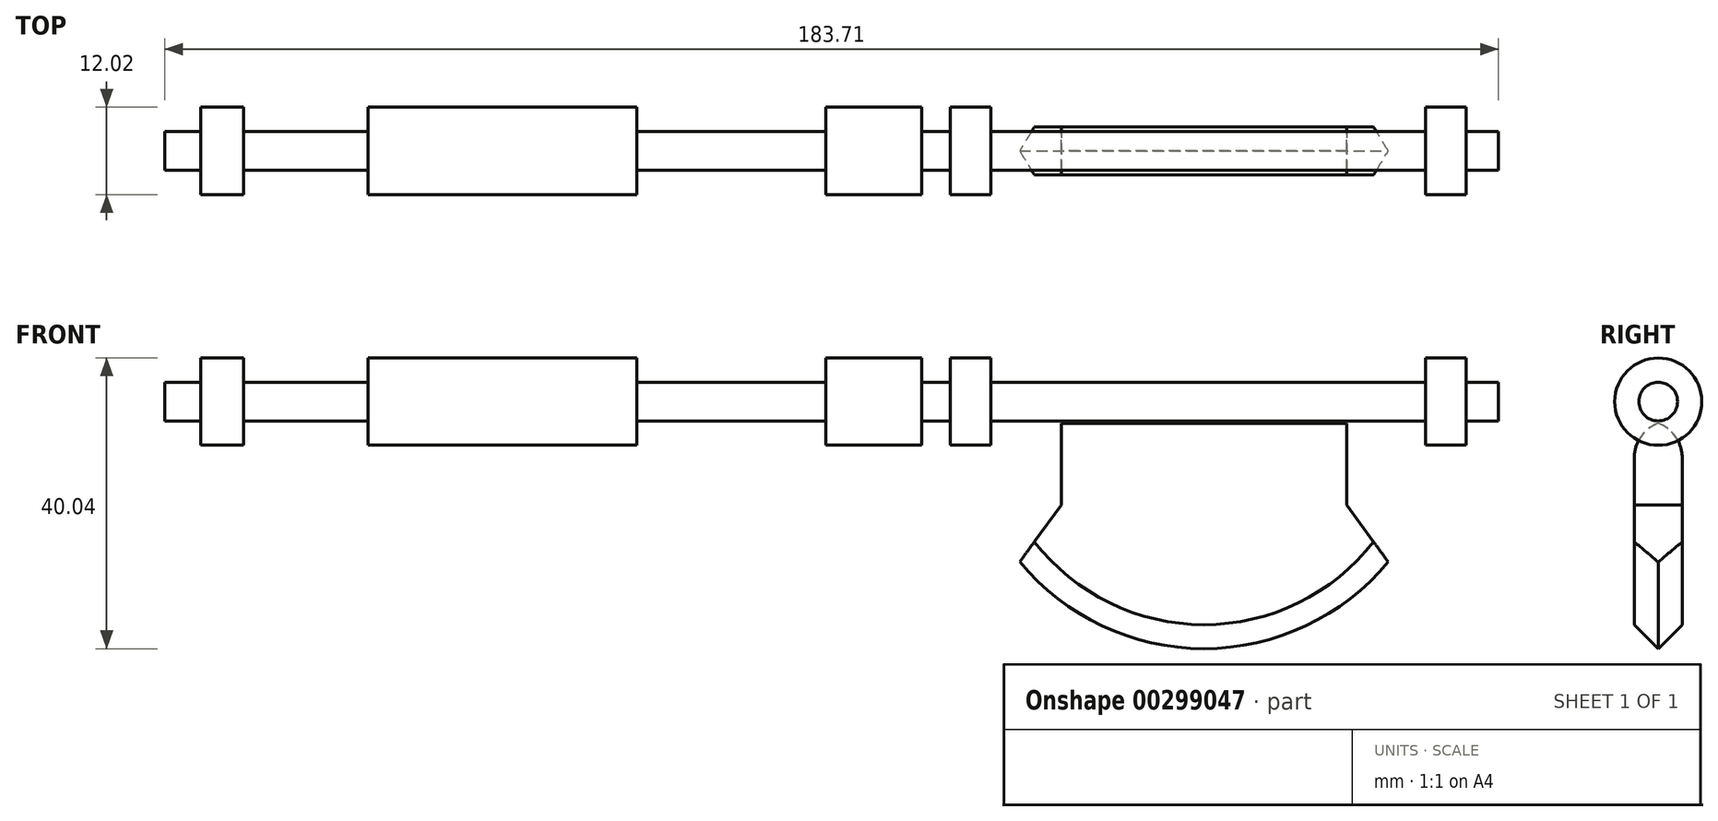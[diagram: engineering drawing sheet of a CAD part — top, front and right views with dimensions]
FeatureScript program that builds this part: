
annotation { "Feature Type Name" : "Feature", "Feature Type Description" : "" }
export const myFeature = defineFeature(function(context is Context, id is Id, definition is map)
    precondition{}
    {
        {
            var Q0;
            Q0=qCreatedBy(makeId("Front.planeOp"),FACE);
            var sketch = newSketch(context, id + "F0", { "sketchPlane" : qUnion([Q0])});
            skLineSegment(sketch, "E0", {"start": v(-57.35, 7.1) * mm, "end": v(-57.35, 12.42) * mm});
            skLineSegment(sketch, "E1", {"start": v(-57.35, 12.42) * mm, "end": v(-52.42, 12.42) * mm});
            skLineSegment(sketch, "E2", {"start": v(-52.42, 12.42) * mm, "end": v(-52.42, 15.77) * mm});
            skLineSegment(sketch, "E3", {"start": v(-46.5, 15.77) * mm, "end": v(-52.42, 15.77) * mm});
            skLineSegment(sketch, "E4", {"start": v(-46.5, 15.77) * mm, "end": v(-46.5, 12.42) * mm});
            skLineSegment(sketch, "E5", {"start": v(-46.5, 12.42) * mm, "end": v(-29.36, 12.42) * mm});
            skLineSegment(sketch, "E6", {"start": v(-29.36, 12.42) * mm, "end": v(-29.36, 15.77) * mm});
            skLineSegment(sketch, "E7", {"start": v(-29.36, 15.77) * mm, "end": v(7.69, 15.77) * mm});
            skLineSegment(sketch, "E8", {"start": v(7.69, 15.77) * mm, "end": v(7.69, 12.42) * mm});
            skLineSegment(sketch, "E9", {"start": v(7.69, 12.42) * mm, "end": v(33.73, 12.42) * mm});
            skLineSegment(sketch, "E10", {"start": v(33.73, 12.42) * mm, "end": v(33.73, 15.77) * mm});
            skLineSegment(sketch, "E11", {"start": v(33.73, 15.77) * mm, "end": v(46.93, 15.77) * mm});
            skLineSegment(sketch, "E12", {"start": v(46.93, 15.77) * mm, "end": v(46.93, 12.42) * mm});
            skLineSegment(sketch, "E13", {"start": v(46.93, 12.42) * mm, "end": v(50.84, 12.42) * mm});
            skLineSegment(sketch, "E14", {"start": v(50.84, 12.42) * mm, "end": v(50.84, 15.77) * mm});
            skLineSegment(sketch, "E15", {"start": v(50.84, 15.77) * mm, "end": v(56.42, 15.77) * mm});
            skLineSegment(sketch, "E16", {"start": v(56.42, 15.77) * mm, "end": v(56.42, 12.42) * mm});
            skLineSegment(sketch, "E17", {"start": v(56.42, 12.42) * mm, "end": v(116.31, 12.42) * mm});
            skLineSegment(sketch, "E18", {"start": v(116.31, 12.42) * mm, "end": v(116.31, 15.77) * mm});
            skLineSegment(sketch, "E19", {"start": v(116.31, 15.77) * mm, "end": v(121.9, 15.77) * mm});
            skLineSegment(sketch, "E20", {"start": v(121.9, 15.77) * mm, "end": v(121.9, 12.42) * mm});
            skLineSegment(sketch, "E21", {"start": v(121.9, 12.42) * mm, "end": v(126.36, 12.42) * mm});
            skLineSegment(sketch, "E22.MirrorCS", {"start": v(56.42, 7.1) * mm, "end": v(116.31, 7.1) * mm});
            skLineSegment(sketch, "E23.MirrorCS", {"start": v(116.31, 7.1) * mm, "end": v(116.31, 3.74) * mm});
            skLineSegment(sketch, "E24.MirrorCS", {"start": v(116.31, 3.74) * mm, "end": v(121.9, 3.74) * mm});
            skLineSegment(sketch, "E25.MirrorCS", {"start": v(121.9, 3.74) * mm, "end": v(121.9, 7.1) * mm});
            skLineSegment(sketch, "E26.MirrorCS", {"start": v(121.9, 7.1) * mm, "end": v(126.36, 7.1) * mm});
            skLineSegment(sketch, "E27.MirrorCS", {"start": v(56.42, 3.74) * mm, "end": v(56.42, 7.1) * mm});
            skLineSegment(sketch, "E28.MirrorCS", {"start": v(50.84, 3.74) * mm, "end": v(56.42, 3.74) * mm});
            skLineSegment(sketch, "E29.MirrorCS", {"start": v(50.84, 7.1) * mm, "end": v(50.84, 3.74) * mm});
            skLineSegment(sketch, "E30.MirrorCS", {"start": v(46.93, 7.1) * mm, "end": v(50.84, 7.1) * mm});
            skLineSegment(sketch, "E31.MirrorCS", {"start": v(46.93, 3.74) * mm, "end": v(46.93, 7.1) * mm});
            skLineSegment(sketch, "E32.MirrorCS", {"start": v(33.73, 3.74) * mm, "end": v(46.93, 3.74) * mm});
            skLineSegment(sketch, "E33.MirrorCS", {"start": v(33.73, 7.1) * mm, "end": v(33.73, 3.74) * mm});
            skLineSegment(sketch, "E34.MirrorCS", {"start": v(7.69, 7.1) * mm, "end": v(33.73, 7.1) * mm});
            skLineSegment(sketch, "E35.MirrorCS", {"start": v(7.69, 3.74) * mm, "end": v(7.69, 7.1) * mm});
            skLineSegment(sketch, "E36.MirrorCS", {"start": v(-29.36, 3.74) * mm, "end": v(7.69, 3.74) * mm});
            skLineSegment(sketch, "E37.MirrorCS", {"start": v(-29.36, 7.1) * mm, "end": v(-29.36, 3.74) * mm});
            skLineSegment(sketch, "E38.MirrorCS", {"start": v(-46.5, 7.1) * mm, "end": v(-29.36, 7.1) * mm});
            skLineSegment(sketch, "E39.MirrorCS", {"start": v(-46.5, 3.74) * mm, "end": v(-46.5, 7.1) * mm});
            skLineSegment(sketch, "E40.MirrorCS", {"start": v(-46.5, 3.74) * mm, "end": v(-52.42, 3.74) * mm});
            skLineSegment(sketch, "E41.MirrorCS", {"start": v(-52.42, 7.1) * mm, "end": v(-52.42, 3.74) * mm});
            skLineSegment(sketch, "E42.MirrorCS", {"start": v(-57.35, 7.1) * mm, "end": v(-52.42, 7.1) * mm});
            skLineSegment(sketch, "E43", {"start": v(126.36, 12.42) * mm, "end": v(126.36, 7.1) * mm});
            skLineSegment(sketch, "E44", {"start": v(-57.35, 9.75) * mm, "end": v(126.36, 9.75) * mm});
            skLineSegment(sketch, "E45", {"start": v(66.13, 7.1) * mm, "end": v(66.13, -4.45) * mm});
            skLineSegment(sketch, "E46", {"start": v(66.13, -4.45) * mm, "end": v(59.34, -13.8) * mm});
            skLineSegment(sketch, "E47", {"start": v(105.45, 7.1) * mm, "end": v(105.45, -4.45) * mm});
            skLineSegment(sketch, "E48", {"start": v(105.45, -4.45) * mm, "end": v(112.25, -13.8) * mm});
            skArc(sketch, "E49", {"start": v(59.34, -13.8) * mm, "mid": v(85.8, -26.04) * mm, "end": v(112.25, -13.8) * mm});
            skSolve(sketch);
        }
        {
            var Q0;
            {var subQ1=sQuery(id+"F0.wireOp",EDGE,"E1");Q0=makeQuery(id+"F0.imprint","IMPRINT",FACE,{"disambiguationData":[TD([[makeQuery(id+"F0.imprint","IMPRINT",EDGE,{"derivedFrom":subQ1}),-1.0]])]});}
            var Q1;
            Q1=sQuery(id+"F0.wireOp",EDGE,"E44");
            revolve(context, id + "F1", {"entities" : qUnion([Q0]), "axis" : qUnion([Q1]), "revolveType" : RevolveType.FULL});
        }
        {
            var Q0;
            {var subQ1=sQuery(id+"F0.wireOp",EDGE,"E45");Q0=makeQuery(id+"F0.imprint","IMPRINT",FACE,{"disambiguationData":[TD([[makeQuery(id+"F0.imprint","IMPRINT",EDGE,{"derivedFrom":subQ1}),1.0]])]});}
            var Q1;
            Q1=sQuery(id+"F0.wireOp",EDGE,"E45");
            var Q2;
            Q2=sQuery(id+"F0.wireOp",EDGE,"E47");
            var Q3;
            Q3=sQuery(id+"F0.wireOp",EDGE,"E48");
            var Q4;
            Q4=sQuery(id+"F0.wireOp",EDGE,"E49");
            var Q5;
            Q5=sQuery(id+"F0.wireOp",EDGE,"E46");
            extrude(context, id + "F2", {"entities" : qUnion([Q0]), "surfaceEntities" : qUnion([Q1, Q2, Q3, Q4, Q5]), "oppositeDirection" : true, "depth" : 3.3 * mm});
        }
        {
            var Q0;
            Q0=makeQuery(id+"F2.opExtrude","CAP_FACE",FACE,{"disambiguationData":[OSD([sQuery(id+"F0.wireOp",EDGE,"E22.MirrorCS"),sQuery(id+"F0.wireOp",EDGE,"E45"),sQuery(id+"F0.wireOp",EDGE,"E46"),sQuery(id+"F0.wireOp",EDGE,"E47"),sQuery(id+"F0.wireOp",EDGE,"E48"),sQuery(id+"F0.wireOp",EDGE,"E49")])],"isStart":true});
            extrude(context, id + "F3", {"entities" : qUnion([Q0]), "operationType" : NewBodyOperationType.ADD, "depth" : 3.3 * mm});
        }
        {
            var Q0;
            Q0=makeQuery(id+"F3.opExtrude","CAP_EDGE",EDGE,{"disambiguationData":[OSD([sQuery(id+"F0.wireOp",EDGE,"E49")])],"isStart":false});
            var Q1;
            Q1=makeQuery(id+"F2.opExtrude","CAP_EDGE",EDGE,{"disambiguationData":[OSD([sQuery(id+"F0.wireOp",EDGE,"E49")])],"isStart":false});
            chamfer(context, id + "F4", {"entities" : qUnion([Q0, Q1]), "width" : 5.08 * mm, "tangentPropagation" : true});
        }
        {
            var Q0;
            Q0=makeQuery(id+"F3.opExtrude","CAP_EDGE",EDGE,{"disambiguationData":[OSD([sQuery(id+"F0.wireOp",EDGE,"E22.MirrorCS")])],"isStart":false});
            var Q1;
            Q1=makeQuery(id+"F2.opExtrude","CAP_EDGE",EDGE,{"disambiguationData":[OSD([sQuery(id+"F0.wireOp",EDGE,"E22.MirrorCS")])],"isStart":false});
            fillet(context, id + "F5", {"entities" : qUnion([Q0, Q1]), "radius" : 5.08 * mm, "tangentPropagation" : true, "allowEdgeOverflow" : false});
        }
    });
